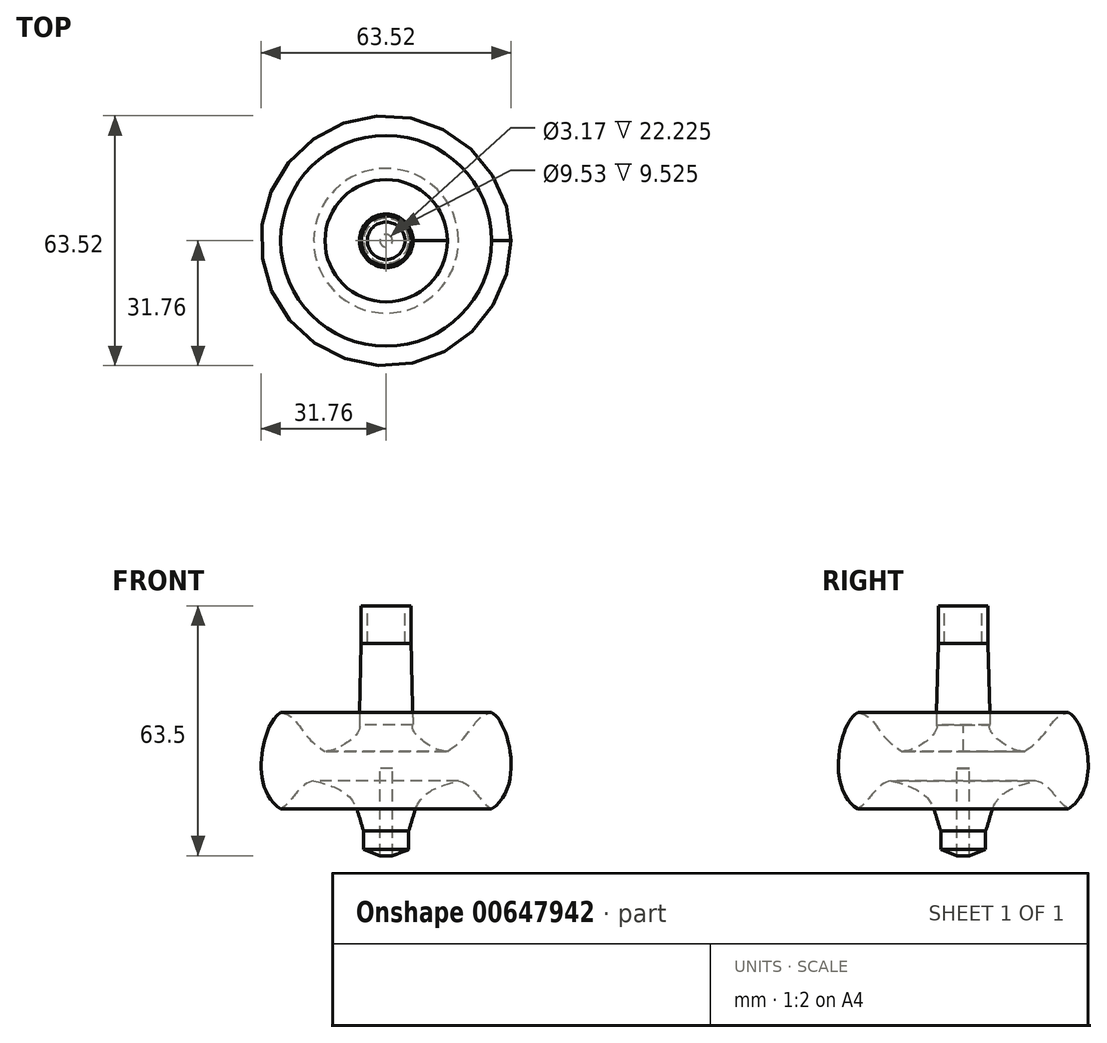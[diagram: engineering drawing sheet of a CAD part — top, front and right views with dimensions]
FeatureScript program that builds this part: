
annotation { "Feature Type Name" : "Feature", "Feature Type Description" : "" }
export const myFeature = defineFeature(function(context is Context, id is Id, definition is map)
    precondition{}
    {
        {
            var Q0;
            Q0=qCreatedBy(makeId("Front.planeOp"),FACE);
            var sketch = newSketch(context, id + "F0", { "sketchPlane" : qUnion([Q0])});
            skLineSegment(sketch, "E0", {"start": v(0, 0) * mm, "end": v(0, 22.23) * mm});
            skLineSegment(sketch, "E1", {"start": v(0, 22.23) * mm, "end": v(1.59, 22.23) * mm});
            skLineSegment(sketch, "E2", {"start": v(1.59, 22.23) * mm, "end": v(1.59, 0) * mm});
            skLineSegment(sketch, "E3", {"start": v(1.59, 0) * mm, "end": v(5.7, 1.56) * mm});
            skLineSegment(sketch, "E4", {"start": v(5.7, 1.56) * mm, "end": v(5.7, 6.28) * mm});
            skFitSpline(sketch, "E5", {"points": [v(5.7, 6.28) * mm, v(18.38, 19.06) * mm], "startDerivative": vector(6.99, 20.09) * mm, "endDerivative": vector(34.07, 8.5) * mm});
            skLineSegment(sketch, "E6", {"start": v(6.33, 53.98) * mm, "end": v(6.33, 63.5) * mm});
            skLineSegment(sketch, "E7", {"start": v(6.33, 63.5) * mm, "end": v(4.76, 63.5) * mm});
            skLineSegment(sketch, "E8", {"start": v(4.76, 63.5) * mm, "end": v(4.76, 53.98) * mm});
            skLineSegment(sketch, "E9", {"start": v(4.76, 53.98) * mm, "end": v(0, 53.98) * mm});
            skLineSegment(sketch, "E10", {"start": v(0, 53.98) * mm, "end": v(0, 0) * mm});
            skFitSpline(sketch, "E11", {"points": [v(18.38, 19.06) * mm, v(26.78, 11.9) * mm], "startDerivative": vector(12, -2.67) * mm, "endDerivative": vector(8.45, -4.54) * mm});
            skFitSpline(sketch, "E12", {"points": [v(26.78, 11.9) * mm, v(26.78, 36.36) * mm], "startDerivative": vector(26.5, 17.17) * mm, "endDerivative": vector(-12.03, 4.79) * mm});
            skFitSpline(sketch, "E13", {"points": [v(15.54, 26.57) * mm, v(26.78, 36.36) * mm], "startDerivative": vector(20.7, 12.18) * mm, "endDerivative": vector(14.67, 2.07) * mm});
            skPoint(sketch, "E14", {"position": v(31.75, 23.49) * mm});
            skLineSegment(sketch, "E15", {"start": v(6.8, 33.27) * mm, "end": v(6.33, 53.98) * mm});
            skFitSpline(sketch, "E16", {"points": [v(15.54, 26.57) * mm, v(6.8, 33.27) * mm], "startDerivative": vector(-10.67, -0.67) * mm, "endDerivative": vector(3.33, 6) * mm});
            skSolve(sketch);
        }
        {
            var Q0;
            Q0 = qSketchRegion(id + "F0", true);
            var Q1;
            Q1=sQuery(id+"F0.wireOp",EDGE,"E10");
            revolve(context, id + "F1", {"entities" : qUnion([Q0]), "axis" : qUnion([Q1]), "revolveType" : RevolveType.FULL});
        }
    });
